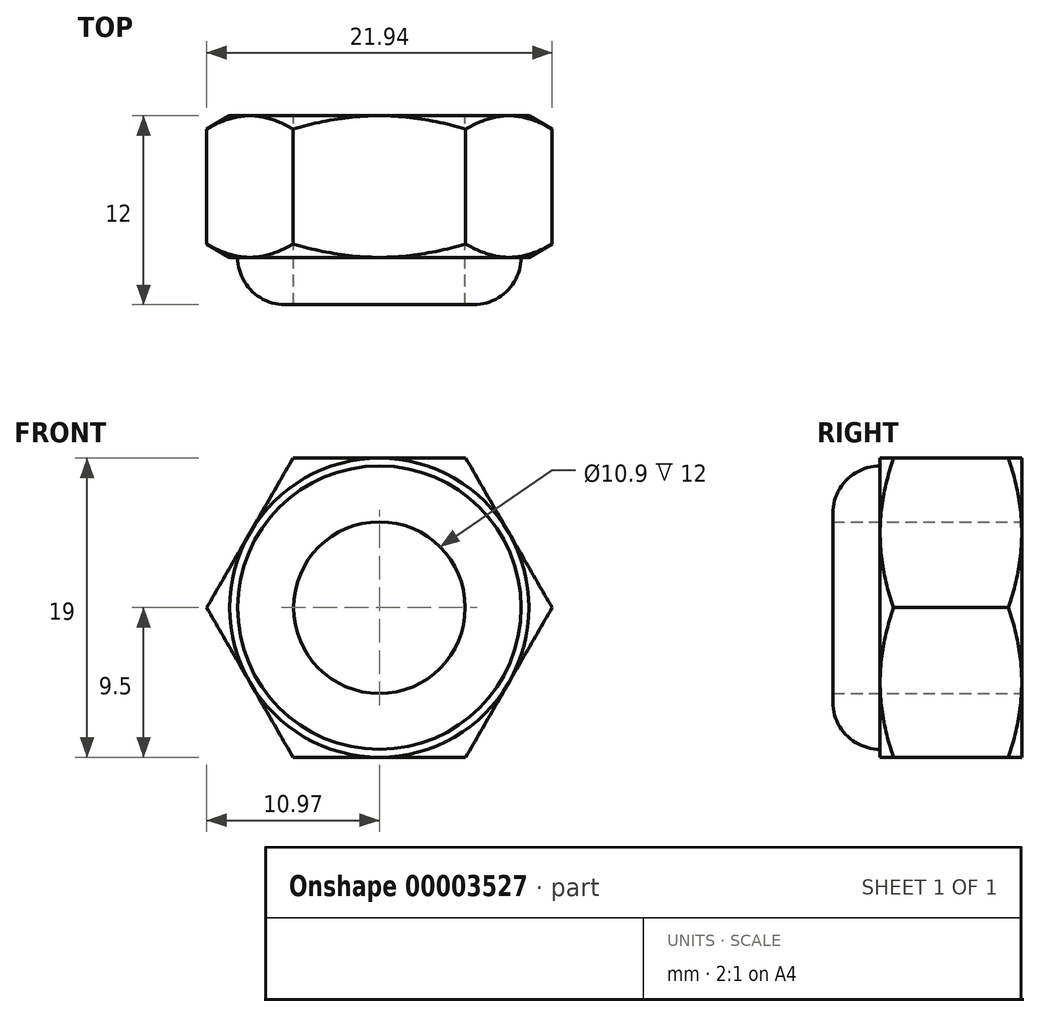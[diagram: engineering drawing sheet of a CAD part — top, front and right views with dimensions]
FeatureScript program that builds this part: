
annotation { "Feature Type Name" : "Feature", "Feature Type Description" : "" }
export const myFeature = defineFeature(function(context is Context, id is Id, definition is map)
    precondition{}
    {
        {
            var Q0;
            Q0=qCreatedBy(makeId("Front.planeOp"),FACE);
            var sketch = newSketch(context, id + "F0", { "sketchPlane" : qUnion([Q0])});
            skCircle(sketch, "E0.cCircle", {"center": v(0, 0) * mm, "radius": 9.5 * mm, "construction": true});
            skLineSegment(sketch, "E0.0", {"start": v(5.48, 9.5) * mm, "end": v(10.97, 0) * mm});
            skLineSegment(sketch, "E0.1", {"start": v(10.97, 0) * mm, "end": v(5.48, -9.5) * mm});
            skLineSegment(sketch, "E0.2", {"start": v(5.48, -9.5) * mm, "end": v(-5.48, -9.5) * mm});
            skLineSegment(sketch, "E0.3", {"start": v(-5.48, -9.5) * mm, "end": v(-10.97, 0) * mm});
            skLineSegment(sketch, "E0.4", {"start": v(-10.97, 0) * mm, "end": v(-5.48, 9.5) * mm});
            skLineSegment(sketch, "E0.5", {"start": v(-5.48, 9.5) * mm, "end": v(5.48, 9.5) * mm});
            skPoint(sketch, "E0.0.midPoint", {"position": v(8.23, 4.75) * mm});
            skCircle(sketch, "E1", {"center": v(0, 0) * mm, "radius": 5.45 * mm});
            skSolve(sketch);
        }
        {
            var Q0;
            Q0=makeQuery(id+"F0.imprint","IMPRINT",FACE,{"disambiguationData":[TD([[makeQuery(id+"F0.imprint","IMPRINT",EDGE,{"derivedFrom":sQuery(id+"F0.wireOp",EDGE,"E0.0")}),-1.0]])]});
            extrude(context, id + "F1", {"entities" : qUnion([Q0]), "depth" : 12 * mm});
        }
        {
            var Q0;
            Q0=qCreatedBy(makeId("Right.planeOp"),FACE);
            var sketch = newSketch(context, id + "F2", { "sketchPlane" : qUnion([Q0])});
            skLineSegment(sketch, "E2", {"start": v(0, 9.5) * mm, "end": v(0, 15) * mm});
            skLineSegment(sketch, "E3", {"start": v(0, 15) * mm, "end": v(-3.18, 15) * mm});
            skLineSegment(sketch, "E4", {"start": v(-3.18, 15) * mm, "end": v(0, 9.5) * mm});
            skLineSegment(sketch, "E5", {"start": v(-5.82, 15) * mm, "end": v(-9, 15) * mm});
            skLineSegment(sketch, "E6", {"start": v(-9, 15) * mm, "end": v(-9, 9.5) * mm});
            skLineSegment(sketch, "E7", {"start": v(-9, 9.5) * mm, "end": v(-5.82, 15) * mm});
            skLineSegment(sketch, "E8", {"start": v(-9, 9.5) * mm, "end": v(-12, 9.5) * mm});
            skLineSegment(sketch, "E9", {"start": v(-12, 9.5) * mm, "end": v(-12, 6) * mm});
            skLineSegment(sketch, "E10", {"start": v(-9, 9.5) * mm, "end": v(-9, 9) * mm});
            skArc(sketch, "E11", {"start": v(-9, 9) * mm, "mid": v(-11.12, 8.12) * mm, "end": v(-12, 6) * mm});
            skLineSegment(sketch, "E12", {"start": v(0, 0) * mm, "end": v(-12.06, 0) * mm});
            skLineSegment(sketch, "E13", {"start": v(-9, 15) * mm, "end": v(-12, 15) * mm});
            skLineSegment(sketch, "E14", {"start": v(-12, 15) * mm, "end": v(-12, 9.5) * mm});
            skSolve(sketch);
        }
        {
            var Q0;
            Q0=makeQuery(id+"F2.imprint","IMPRINT",FACE,{"disambiguationData":[TD([[makeQuery(id+"F2.imprint","IMPRINT",EDGE,{"derivedFrom":sQuery(id+"F2.wireOp",EDGE,"E8")}),1.0]])]});
            var Q1;
            Q1=makeQuery(id+"F2.imprint","IMPRINT",FACE,{"disambiguationData":[TD([[makeQuery(id+"F2.imprint","IMPRINT",EDGE,{"derivedFrom":sQuery(id+"F2.wireOp",EDGE,"E5")}),1.0]])]});
            var Q2;
            Q2=makeQuery(id+"F2.imprint","IMPRINT",FACE,{"disambiguationData":[TD([[makeQuery(id+"F2.imprint","IMPRINT",EDGE,{"derivedFrom":sQuery(id+"F2.wireOp",EDGE,"E2")}),1.0]])]});
            var Q3;
            Q3=makeQuery(id+"F2.imprint","IMPRINT",FACE,{"disambiguationData":[TD([[makeQuery(id+"F2.imprint","IMPRINT",EDGE,{"derivedFrom":sQuery(id+"F2.wireOp",EDGE,"E6")}),-1.0]])]});
            var Q4;
            Q4=sQuery(id+"F2.wireOp",EDGE,"E12");
            revolve(context, id + "F3", {"operationType" : NewBodyOperationType.REMOVE, "entities" : qUnion([Q0, Q1, Q2, Q3]), "axis" : qUnion([Q4]), "revolveType" : RevolveType.FULL});
        }
    });
